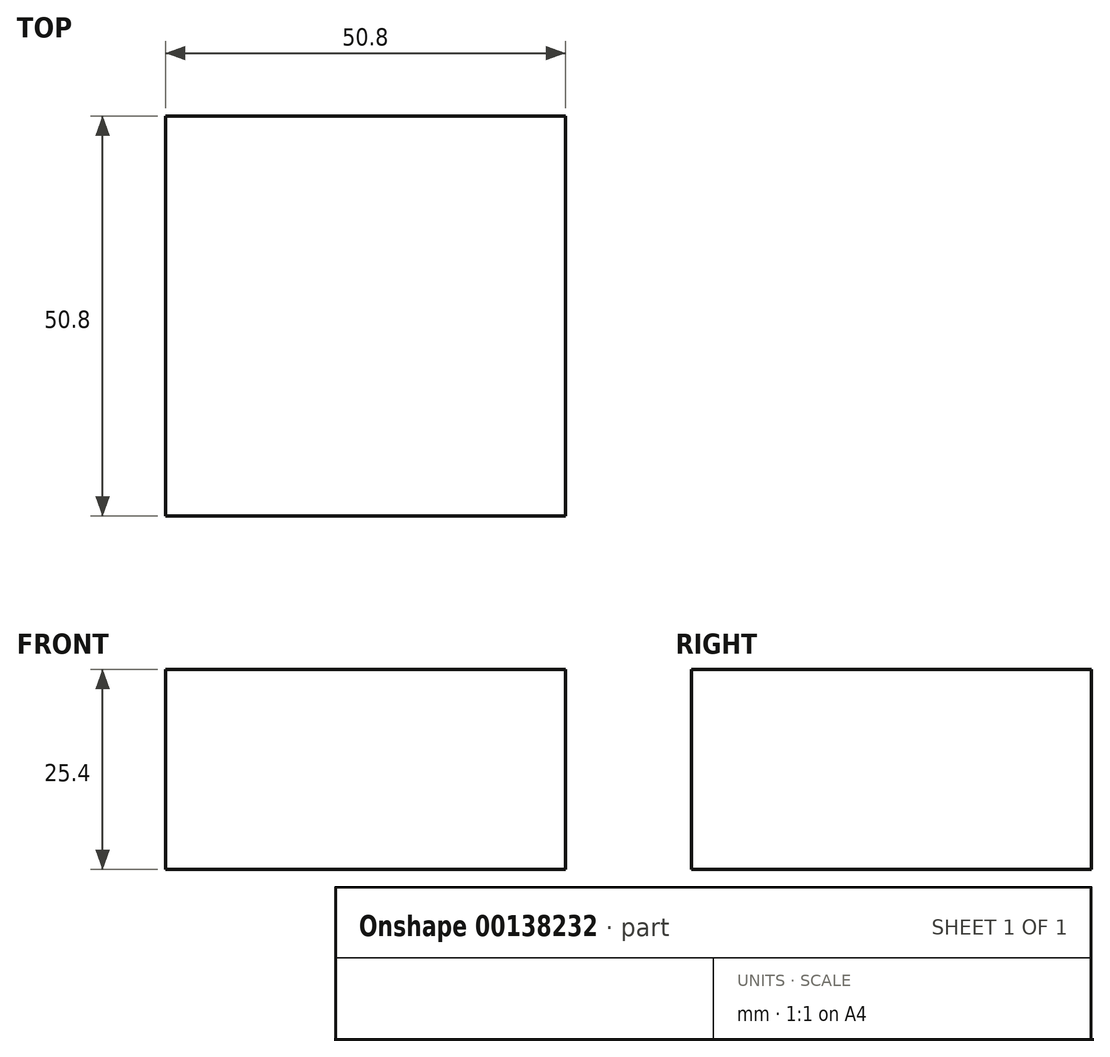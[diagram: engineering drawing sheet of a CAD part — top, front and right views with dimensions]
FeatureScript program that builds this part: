
annotation { "Feature Type Name" : "Feature", "Feature Type Description" : "" }
export const myFeature = defineFeature(function(context is Context, id is Id, definition is map)
    precondition{}
    {
        {
            var Q0;
            Q0=qCreatedBy(makeId("Front.planeOp"),FACE);
            var sketch = newSketch(context, id + "F0", { "sketchPlane" : qUnion([Q0])});
            skLineSegment(sketch, "E0.bottom", {"start": v(25.4, 12.7) * mm, "end": v(-25.4, 12.7) * mm});
            skLineSegment(sketch, "E0.top", {"start": v(25.4, -12.7) * mm, "end": v(-25.4, -12.7) * mm});
            skLineSegment(sketch, "E0.left", {"start": v(25.4, 12.7) * mm, "end": v(25.4, -12.7) * mm});
            skLineSegment(sketch, "E0.right", {"start": v(-25.4, 12.7) * mm, "end": v(-25.4, -12.7) * mm});
            skPoint(sketch, "E0.middle", {"position": v(0, 0) * mm});
            skSolve(sketch);
        }
        {
            var Q0;
            Q0 = qSketchRegion(id + "F0", true);
            extrude(context, id + "F1", {"entities" : qUnion([Q0]), "depth" : 50.8 * mm});
        }
    });
